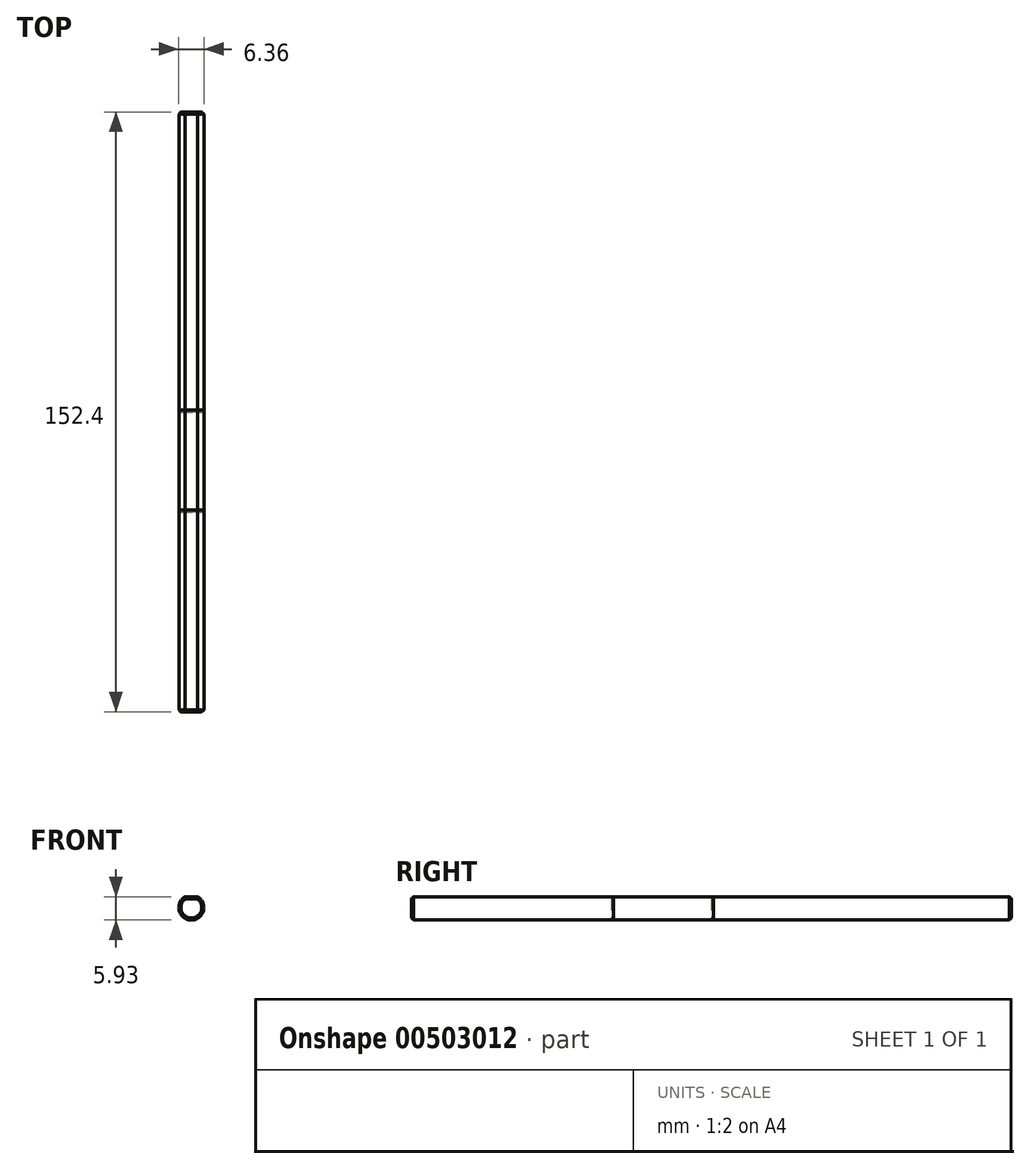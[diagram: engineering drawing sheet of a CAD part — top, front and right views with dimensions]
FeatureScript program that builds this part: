
annotation { "Feature Type Name" : "Feature", "Feature Type Description" : "" }
export const myFeature = defineFeature(function(context is Context, id is Id, definition is map)
    precondition{}
    {
        {
            var Q0;
            Q0=qCreatedBy(makeId("Front.planeOp"),FACE);
            var sketch = newSketch(context, id + "F0", { "sketchPlane" : qUnion([Q0])});
            skArc(sketch, "E0", {"start": v(-1.59, 2.75) * mm, "mid": v(0, -3.18) * mm, "end": v(1.59, 2.75) * mm});
            skLineSegment(sketch, "E1", {"start": v(-1.59, 2.75) * mm, "end": v(1.59, 2.75) * mm});
            skSolve(sketch);
        }
        {
            var Q0;
            Q0=makeQuery(id+"F0.imprint","IMPRINT",FACE,{"disambiguationData":[TD([[makeQuery(id+"F0.imprint","IMPRINT",EDGE,{"derivedFrom":sQuery(id+"F0.wireOp",EDGE,"E0")}),1.0]])]});
            extrude(context, id + "F1", {"entities" : qUnion([Q0]), "depth" : 152.4 * mm});
        }
        {
            var Q0;
            Q0 = qSketchRegion(id + "F0", true);
            extrude(context, id + "F2", {"entities" : qUnion([Q0]), "depth" : 76.2 * mm, "offsetDistance" : 25.4 * mm});
        }
        {
            var Q0;
            Q0 = qSketchRegion(id + "F0", true);
            extrude(context, id + "F3", {"entities" : qUnion([Q0]), "depth" : 101.6 * mm, "offsetDistance" : 25.4 * mm});
        }
        {
            var Q0;
            Q0=makeQuery(id+"F1.opExtrude","CAP_FACE",FACE,{"disambiguationData":[OSD([sQuery(id+"F0.wireOp",EDGE,"E0"),sQuery(id+"F0.wireOp",EDGE,"E1")])],"isStart":true});
            var Q1;
            Q1=makeQuery(id+"F1.opExtrude","CAP_FACE",FACE,{"disambiguationData":[OSD([sQuery(id+"F0.wireOp",EDGE,"E0"),sQuery(id+"F0.wireOp",EDGE,"E1")])],"isStart":false});
            var Q2;
            Q2=makeQuery(id+"F2.opExtrude","CAP_FACE",FACE,{"disambiguationData":[OSD([sQuery(id+"F0.wireOp",EDGE,"E0"),sQuery(id+"F0.wireOp",EDGE,"E1")])],"isStart":false});
            var Q3;
            Q3=makeQuery(id+"F2.opExtrude","CAP_FACE",FACE,{"disambiguationData":[OSD([sQuery(id+"F0.wireOp",EDGE,"E0"),sQuery(id+"F0.wireOp",EDGE,"E1")])],"isStart":true});
            var Q4;
            Q4=makeQuery(id+"F3.opExtrude","CAP_FACE",FACE,{"disambiguationData":[OSD([sQuery(id+"F0.wireOp",EDGE,"E0"),sQuery(id+"F0.wireOp",EDGE,"E1")])],"isStart":false});
            var Q5;
            Q5=makeQuery(id+"F3.opExtrude","CAP_FACE",FACE,{"disambiguationData":[OSD([sQuery(id+"F0.wireOp",EDGE,"E0"),sQuery(id+"F0.wireOp",EDGE,"E1")])],"isStart":true});
            chamfer(context, id + "F4", {"entities" : qUnion([Q0, Q1, Q2, Q3, Q4, Q5]), "width" : 0.5 * mm, "tangentPropagation" : true});
        }
    });
